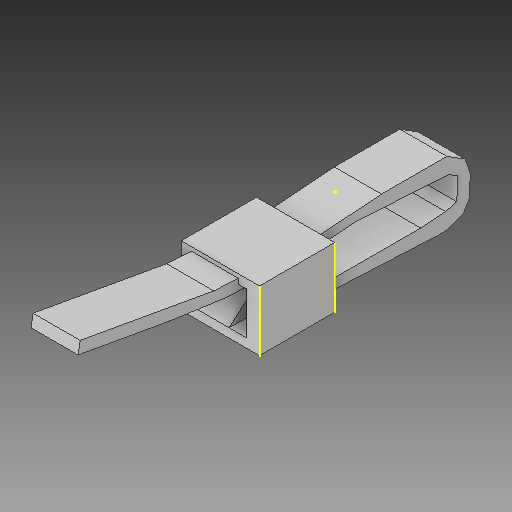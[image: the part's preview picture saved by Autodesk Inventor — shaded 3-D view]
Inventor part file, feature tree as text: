
AUTODESK INVENTOR PART (.ipt)
format: ipt  version: 2018 (Build 220112000, 112)  size: 148,480 bytes
history: native  units: mm
features: sketch x4, extrude x3
ambient origin geometry x8: Origin, YZ Plane, XZ Plane, XY Plane, X Axis, Y Axis, Z Axis, Center Point
bodies: Solid1 (feature_tree)
feature tree (7):
  extrude  "Extrusion1"  Depth=2.5mm TaperAngle=0.0deg
  sketch  "Sketch3"  dims[d4=2.0mm d5=0.0mm]
  extrude  "Extrusion2"  [1 undecoded]
  extrude  "Extrusion3"  [1 undecoded]
  sketch  "Sketch1"  dims[d0=4.0mm d1=0.0mm d2=2.5mm d3=0.0mm]
  sketch  "Sketch4"
  sketch  "Sketch5"
note: 2 required parameter values undecoded (feature->parameter linkage not recoverable at this tier; creation-order binding heuristic only, values carry confidence <= 0.55)
